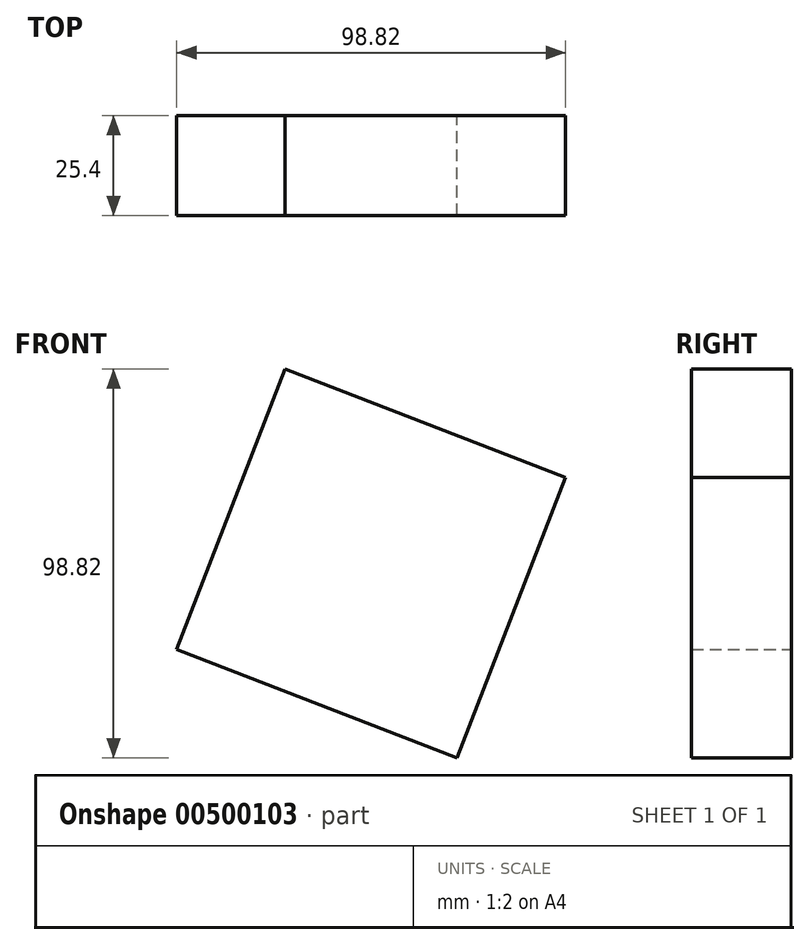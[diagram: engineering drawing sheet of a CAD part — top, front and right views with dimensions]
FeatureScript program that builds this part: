
annotation { "Feature Type Name" : "Feature", "Feature Type Description" : "" }
export const myFeature = defineFeature(function(context is Context, id is Id, definition is map)
    precondition{}
    {
        {
            var Q0;
            Q0=qCreatedBy(makeId("Front.planeOp"),FACE);
            var sketch = newSketch(context, id + "F0", { "sketchPlane" : qUnion([Q0])});
            skCircle(sketch, "E0.cCircle", {"center": v(0, 0) * mm, "radius": 54.03 * mm, "construction": true});
            skLineSegment(sketch, "E0.0", {"start": v(21.86, -49.4) * mm, "end": v(-49.4, -21.86) * mm});
            skLineSegment(sketch, "E0.1", {"start": v(-49.4, -21.86) * mm, "end": v(-21.86, 49.4) * mm});
            skLineSegment(sketch, "E0.2", {"start": v(-21.86, 49.4) * mm, "end": v(49.4, 21.86) * mm});
            skLineSegment(sketch, "E0.3", {"start": v(49.4, 21.86) * mm, "end": v(21.86, -49.4) * mm});
            skSolve(sketch);
        }
        {
            var Q0;
            Q0 = qSketchRegion(id + "F0", true);
            extrude(context, id + "F1", {"entities" : qUnion([Q0]), "endBound" : BoundingType.SYMMETRIC, "depth" : 25.4 * mm});
        }
    });
